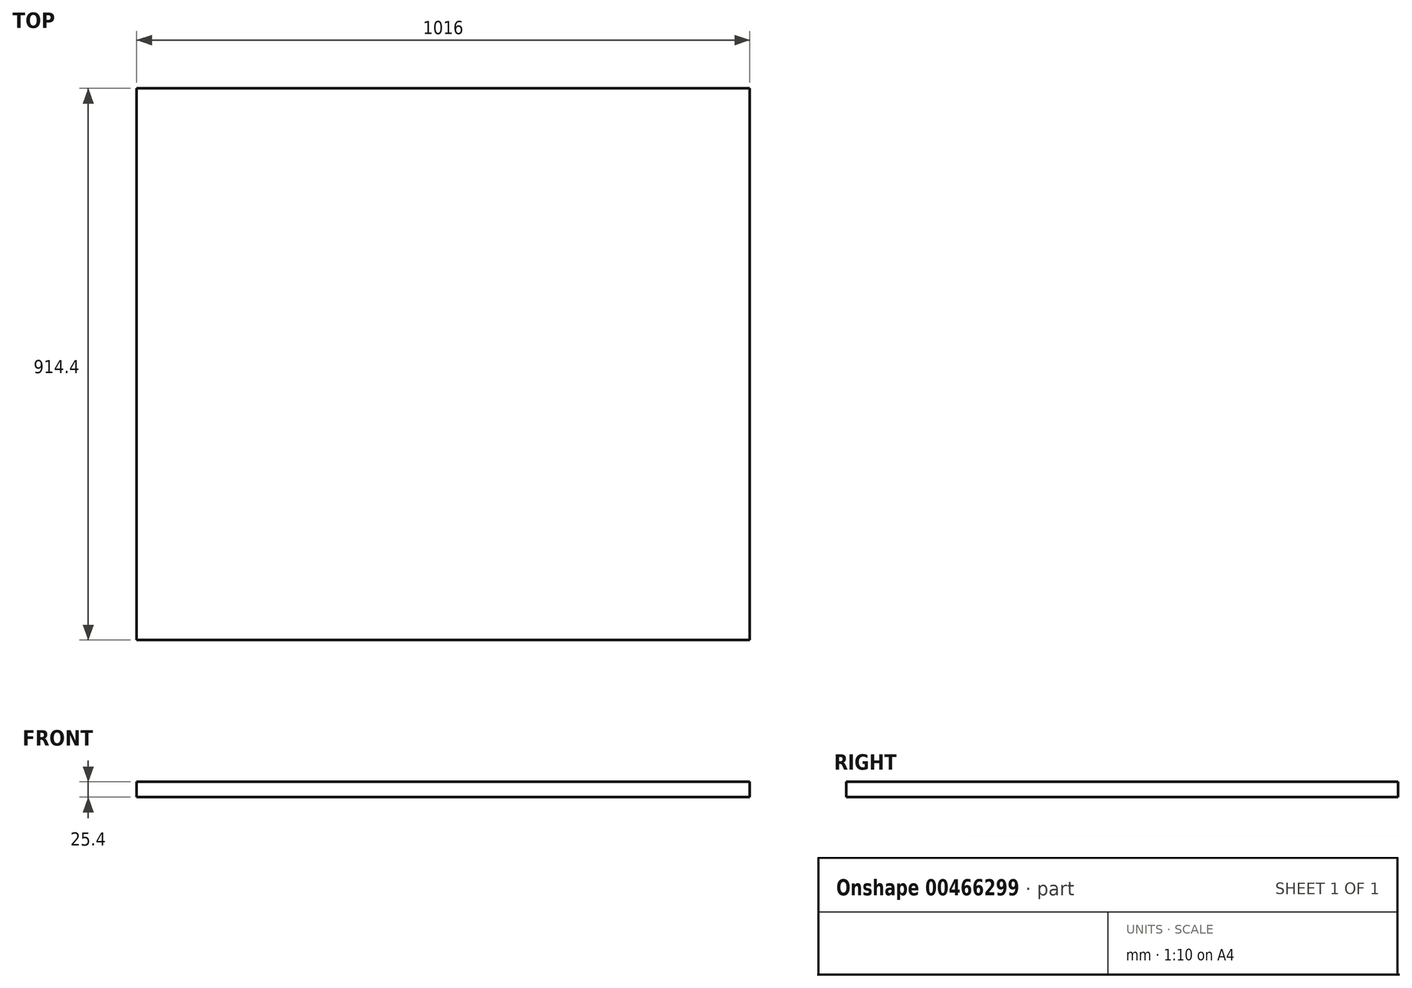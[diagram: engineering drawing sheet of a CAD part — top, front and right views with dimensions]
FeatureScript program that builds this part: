
annotation { "Feature Type Name" : "Feature", "Feature Type Description" : "" }
export const myFeature = defineFeature(function(context is Context, id is Id, definition is map)
    precondition{}
    {
        {
            var Q0;
            Q0=qCreatedBy(makeId("Top.planeOp"),FACE);
            var sketch = newSketch(context, id + "F0", { "sketchPlane" : qUnion([Q0])});
            skLineSegment(sketch, "E0.bottom", {"start": v(508, 457.2) * mm, "end": v(-508, 457.2) * mm});
            skLineSegment(sketch, "E0.top", {"start": v(508, -457.2) * mm, "end": v(-508, -457.2) * mm});
            skLineSegment(sketch, "E0.left", {"start": v(508, 457.2) * mm, "end": v(508, -457.2) * mm});
            skLineSegment(sketch, "E0.right", {"start": v(-508, 457.2) * mm, "end": v(-508, -457.2) * mm});
            skPoint(sketch, "E0.middle", {"position": v(0, 0) * mm});
            skSolve(sketch);
        }
        {
            var Q0;
            Q0=makeQuery(id+"F0.imprint","IMPRINT",FACE,{"disambiguationData":[TD([[makeQuery(id+"F0.imprint","IMPRINT",EDGE,{"derivedFrom":sQuery(id+"F0.wireOp",EDGE,"E0.bottom")}),1.0]])]});
            extrude(context, id + "F1", {"entities" : qUnion([Q0]), "oppositeDirection" : true, "depth" : 25.4 * mm});
        }
    });
